# Revit family: Casement_41_I_Top_Hung_SD_Standard
name_source: partatom
category: Windows
revit_build: Autodesk Revit 2014 (Build: 20130308_1515(x64)
units: mm (PartAtom-declared; Revit-internal decimal feet)

## types (24) — shared parameters
Corrected Mullion Configuration = 2 mm  [stored 0.00656168 ft]
Custom Sash Height = 525 mm
Description = Window 41mm, Type I, Top hung, Standard sash
Frame Profile Thickness = 41 mm  [stored 0.134514 ft]
Heavy Duty Sash = No
Limit Fixed Pane Height Max = 3300 mm  [stored 10.8268 ft]
Limit Fixed Pane Height Min = 200 mm  [stored 0.656168 ft]
Limit Fixed Pane Width Max = 3000 mm  [stored 9.84252 ft]
Limit Fixed Pane Width Min = 200 mm  [stored 0.656168 ft]
Limit Sash Height Max = 1200 mm  [stored 3.93701 ft]
Limit Sash Height Min = 300 mm  [stored 0.984252 ft]
Limit Sash Width Max = 1500 mm  [stored 4.92126 ft]
Limit Sash Width Min = 300 mm  [stored 0.984252 ft]
Manufacturer = Crealco
Max System DG Unit Thickness = 25 mm  [stored 0.082021 ft]
Model = Casement 41
Rough Width = 3 mm  [stored 0.00984252 ft]
Sash Side Gap = 44 mm
Standard Mullion Different = No
Standard Sash = Yes
URL = http://www.crealco.co.za
Wall Closure = By host
zero-valued in all types: Custom Frame Offset From Exterior

## per-type parameters (varying)
| type | Clearvue Insulated LowE SHGC Value | Clearvue Insulated LowE U Value | Clearvue Insulated SHGC Value | Clearvue Insulated U Value | Clearvue SHGC Value | Clearvue U Value | Custom Sash Width | Custom Windload | Custom Window Height | Custom Window Width | Energy Advantage SHGC Value | Energy Advantage U Value | Intruderprufe Insulated LowE SHGC Value | Intruderprufe Insulated LowE U Value | Intruderprufe Insulated SHGC Value | Intruderprufe Insulated U Value | Intruderprufe LowE SHGC Value | Intruderprufe LowE U Value | Intruderprufe SHGC Value | Intruderprufe U Value | Toughened Safety SHGC Value | Toughened Safety U Value |
| 41-1215DT-SD-1000Pa | 0.704 | 4.4 | 0.704 | 4.49 | 0.56 | 6.06 | 525 mm | 1000 mm  [stored 3.28084 ft] | 1490 mm  [stored 4.88845 ft] | 1190 mm  [stored 3.9042 ft] | 0.502 | 4.7 | 0.585 | 3.25 | 0.586 | 3.43 | 0.467 | 4.55 | 0.527 | 5.78 | 0.56 | 6.06 |
| 41-1215DT-SD-1500Pa | 0.704 | 4.4 | 0.704 | 4.49 | 0.56 | 6.06 | 525 mm | 1500 mm  [stored 4.92126 ft] | 1490 mm  [stored 4.88845 ft] | 1190 mm  [stored 3.9042 ft] | 0.502 | 4.7 | 0.585 | 3.25 | 0.586 | 3.43 | 0.467 | 4.55 | 0.527 | 5.78 | 0.56 | 6.06 |
| 41-1215DT-SD-2000Pa | 0.705 | 4.53 | 0.705 | 4.62 | 0.551 | 6.13 | 525 mm | 2000 mm  [stored 6.56168 ft] | 1490 mm  [stored 4.88845 ft] | 1190 mm  [stored 3.9042 ft] | 0.495 | 4.81 | 0.586 | 3.38 | 0.587 | 3.56 | 0.46 | 4.64 | 0.518 | 5.84 | 0.551 | 6.13 |
| 41-1515DT-SD-2000Pa | 0.734 | 4.7 | 0.734 | 4.77 | 0.598 | 6.09 | 525 mm | 2000 mm  [stored 6.56168 ft] | 1490 mm  [stored 4.88845 ft] | 1490 mm  [stored 4.88845 ft] | 0.537 | 4.64 | 0.61 | 3.36 | 0.611 | 3.51 | 0.499 | 4.48 | 0.563 | 5.82 | 0.598 | 6.09 |
| 41-1515DT-SD-1000Pa | 0.733 | 4.59 | 0.733 | 4.67 | 0.606 | 6.04 | 525 mm | 1000 mm  [stored 3.28084 ft] | 1490 mm  [stored 4.88845 ft] | 1490 mm  [stored 4.88845 ft] | 0.543 | 4.55 | 0.609 | 3.26 | 0.61 | 3.41 | 0.505 | 4.4 | 0.57 | 5.78 | 0.606 | 6.04 |
| 41-1515DT-SD-1500Pa | 0.733 | 4.59 | 0.733 | 4.67 | 0.606 | 6.04 | 525 mm | 1500 mm  [stored 4.92126 ft] | 1490 mm  [stored 4.88845 ft] | 1490 mm  [stored 4.88845 ft] | 0.543 | 4.55 | 0.609 | 3.26 | 0.61 | 3.41 | 0.505 | 4.4 | 0.57 | 5.78 | 0.606 | 6.04 |
| 41-1815DT-SD-1000Pa | 0.729 | 4.6 | 0.729 | 4.68 | 0.608 | 6.04 | 825 mm | 1000 mm  [stored 3.28084 ft] | 1490 mm  [stored 4.88845 ft] | 1790 mm  [stored 5.8727 ft] | 0.545 | 4.51 | 0.606 | 3.28 | 0.606 | 3.46 | 0.507 | 4.37 | 0.572 | 5.76 | 0.608 | 6.04 |
| 41-1815DT-SD-1500Pa | 0.73 | 4.69 | 0.73 | 4.77 | 0.602 | 6.09 | 825 mm | 1500 mm  [stored 4.92126 ft] | 1490 mm  [stored 4.88845 ft] | 1790 mm  [stored 5.8727 ft] | 0.54 | 4.58 | 0.606 | 3.37 | 0.607 | 3.55 | 0.502 | 4.43 | 0.567 | 5.8 | 0.602 | 6.09 |
| 41-1815DT-SD-2000Pa | 0.73 | 4.69 | 0.73 | 4.77 | 0.602 | 6.09 | 825 mm | 2000 mm  [stored 6.56168 ft] | 1490 mm  [stored 4.88845 ft] | 1790 mm  [stored 5.8727 ft] | 0.54 | 4.58 | 0.606 | 3.37 | 0.607 | 3.55 | 0.502 | 4.43 | 0.567 | 5.8 | 0.602 | 6.09 |
| 41-2415DT-SD-1000Pa | 0.759 | 4.8 | 0.759 | 4.85 | 0.653 | 6.01 | 825 mm | 1000 mm  [stored 3.28084 ft] | 1490 mm  [stored 4.88845 ft] | 2390 mm  [stored 7.84121 ft] | 0.585 | 4.38 | 0.631 | 3.29 | 0.631 | 3.43 | 0.543 | 4.24 | 0.614 | 5.75 | 0.653 | 6.01 |
| 41-2415DT-SD-1500Pa | 0.76 | 4.86 | 0.76 | 4.92 | 0.649 | 6.05 | 825 mm | 1500 mm  [stored 4.92126 ft] | 1490 mm  [stored 4.88845 ft] | 2390 mm  [stored 7.84121 ft] | 0.581 | 4.43 | 0.631 | 3.35 | 0.632 | 3.49 | 0.54 | 4.28 | 0.61 | 5.78 | 0.649 | 6.05 |
| 41-2415DT-SD-2000Pa | 0.76 | 4.86 | 0.76 | 4.92 | 0.649 | 6.05 | 825 mm | 2000 mm  [stored 6.56168 ft] | 1490 mm  [stored 4.88845 ft] | 2390 mm  [stored 7.84121 ft] | 0.581 | 4.43 | 0.631 | 3.35 | 0.632 | 3.49 | 0.54 | 4.28 | 0.61 | 5.78 | 0.649 | 6.05 |
| 41-1218DT-SD-1000Pa | 0.716 | 4.49 | 0.716 | 4.58 | 0.584 | 6.05 | 525 mm | 1000 mm  [stored 3.28084 ft] | 1790 mm  [stored 5.8727 ft] | 1190 mm  [stored 3.9042 ft] | 0.524 | 4.63 | 0.595 | 3.27 | 0.596 | 3.43 | 0.487 | 4.48 | 0.549 | 5.78 | 0.584 | 6.05 |
| 41-1218DT-SD-1500Pa | 0.718 | 4.63 | 0.718 | 4.71 | 0.571 | 6.12 | 525 mm | 1500 mm  [stored 4.92126 ft] | 1790 mm  [stored 5.8727 ft] | 1190 mm  [stored 3.9042 ft] | 0.512 | 4.76 | 0.597 | 3.4 | 0.597 | 3.56 | 0.476 | 4.59 | 0.537 | 5.84 | 0.571 | 6.12 |
| 41-1218DT-SD-2000Pa | 0.718 | 4.63 | 0.718 | 4.71 | 0.571 | 6.12 | 525 mm | 2000 mm  [stored 6.56168 ft] | 1790 mm  [stored 5.8727 ft] | 1190 mm  [stored 3.9042 ft] | 0.512 | 4.76 | 0.597 | 3.4 | 0.597 | 3.56 | 0.476 | 4.59 | 0.537 | 5.84 | 0.571 | 6.12 |
| 41-1518DT-SD-1000Pa | 0.744 | 4.76 | 0.744 | 4.86 | 0.616 | 6.08 | 525 mm | 1000 mm  [stored 3.28084 ft] | 1790 mm  [stored 5.8727 ft] | 1490 mm  [stored 4.88845 ft] | 0.553 | 4.59 | 0.619 | 3.52 | 0.619 | 3.52 | 0.514 | 4.43 | 0.58 | 5.82 | 0.616 | 6.08 |
| 41-1518DT-SD-1500Pa | 0.744 | 4.76 | 0.744 | 4.86 | 0.616 | 6.08 | 525 mm | 1500 mm  [stored 4.92126 ft] | 1790 mm  [stored 5.8727 ft] | 1490 mm  [stored 4.88845 ft] | 0.553 | 4.59 | 0.619 | 3.52 | 0.619 | 3.52 | 0.514 | 4.43 | 0.58 | 5.82 | 0.616 | 6.08 |
| 41-1518DT-SD-2000Pa | 0.744 | 4.76 | 0.744 | 4.86 | 0.616 | 6.08 | 525 mm | 2000 mm  [stored 6.56168 ft] | 1790 mm  [stored 5.8727 ft] | 1490 mm  [stored 4.88845 ft] | 0.553 | 4.59 | 0.619 | 3.52 | 0.619 | 3.52 | 0.514 | 4.43 | 0.58 | 5.82 | 0.616 | 6.08 |
| 41-1818DT-SD-1000Pa | 0.742 | 4.8 | 0.742 | 4.87 | 0.624 | 6.07 | 825 mm | 1000 mm  [stored 3.28084 ft] | 1790 mm  [stored 5.8727 ft] | 1790 mm  [stored 5.8727 ft] | 0.559 | 4.52 | 0.617 | 3.4 | 0.617 | 3.55 | 0.519 | 4.38 | 0.587 | 5.8 | 0.624 | 6.07 |
| 41-1818DT-SD-1500Pa | 0.742 | 4.8 | 0.742 | 4.87 | 0.624 | 6.07 | 825 mm | 1500 mm  [stored 4.92126 ft] | 1790 mm  [stored 5.8727 ft] | 1790 mm  [stored 5.8727 ft] | 0.559 | 4.52 | 0.617 | 3.4 | 0.617 | 3.55 | 0.519 | 4.38 | 0.587 | 5.8 | 0.624 | 6.07 |
| 41-1818DT-SD-2000Pa | 0.742 | 4.8 | 0.742 | 4.87 | 0.624 | 6.07 | 825 mm | 2000 mm  [stored 6.56168 ft] | 1790 mm  [stored 5.8727 ft] | 1790 mm  [stored 5.8727 ft] | 0.559 | 4.52 | 0.617 | 3.4 | 0.617 | 3.55 | 0.519 | 4.38 | 0.587 | 5.8 | 0.624 | 6.07 |
| 41-2418DT-SD-1000Pa | 0.769 | 4.97 | 0.769 | 5.02 | 0.667 | 6.04 | 825 mm | 1000 mm  [stored 3.28084 ft] | 1790 mm  [stored 5.8727 ft] | 2390 mm  [stored 7.84121 ft] | 0.598 | 4.37 | 0.639 | 3.39 | 0.639 | 3.51 | 0.555 | 4.23 | 0.628 | 5.79 | 0.667 | 6.04 |
| 41-2418DT-SD-1500Pa | 0.769 | 4.97 | 0.769 | 5.02 | 0.667 | 6.04 | 825 mm | 1500 mm  [stored 4.92126 ft] | 1790 mm  [stored 5.8727 ft] | 2390 mm  [stored 7.84121 ft] | 0.598 | 4.37 | 0.639 | 3.39 | 0.639 | 3.51 | 0.555 | 4.23 | 0.628 | 5.79 | 0.667 | 6.04 |
| 41-2418DT-SD-2000Pa | 0.769 | 4.97 | 0.769 | 5.02 | 0.667 | 6.04 | 825 mm | 2000 mm  [stored 6.56168 ft] | 1790 mm  [stored 5.8727 ft] | 2390 mm  [stored 7.84121 ft] | 0.598 | 4.37 | 0.639 | 3.39 | 0.639 | 3.51 | 0.555 | 4.23 | 0.628 | 5.79 | 0.667 | 6.04 |

note: [stored X ft] marks values corroborated as IEEE doubles in the binary element streams (Revit-internal decimal feet)

## geometry (parser evidence)
native form markers: Sweep x15
no freeform markers — native parametric forms only
